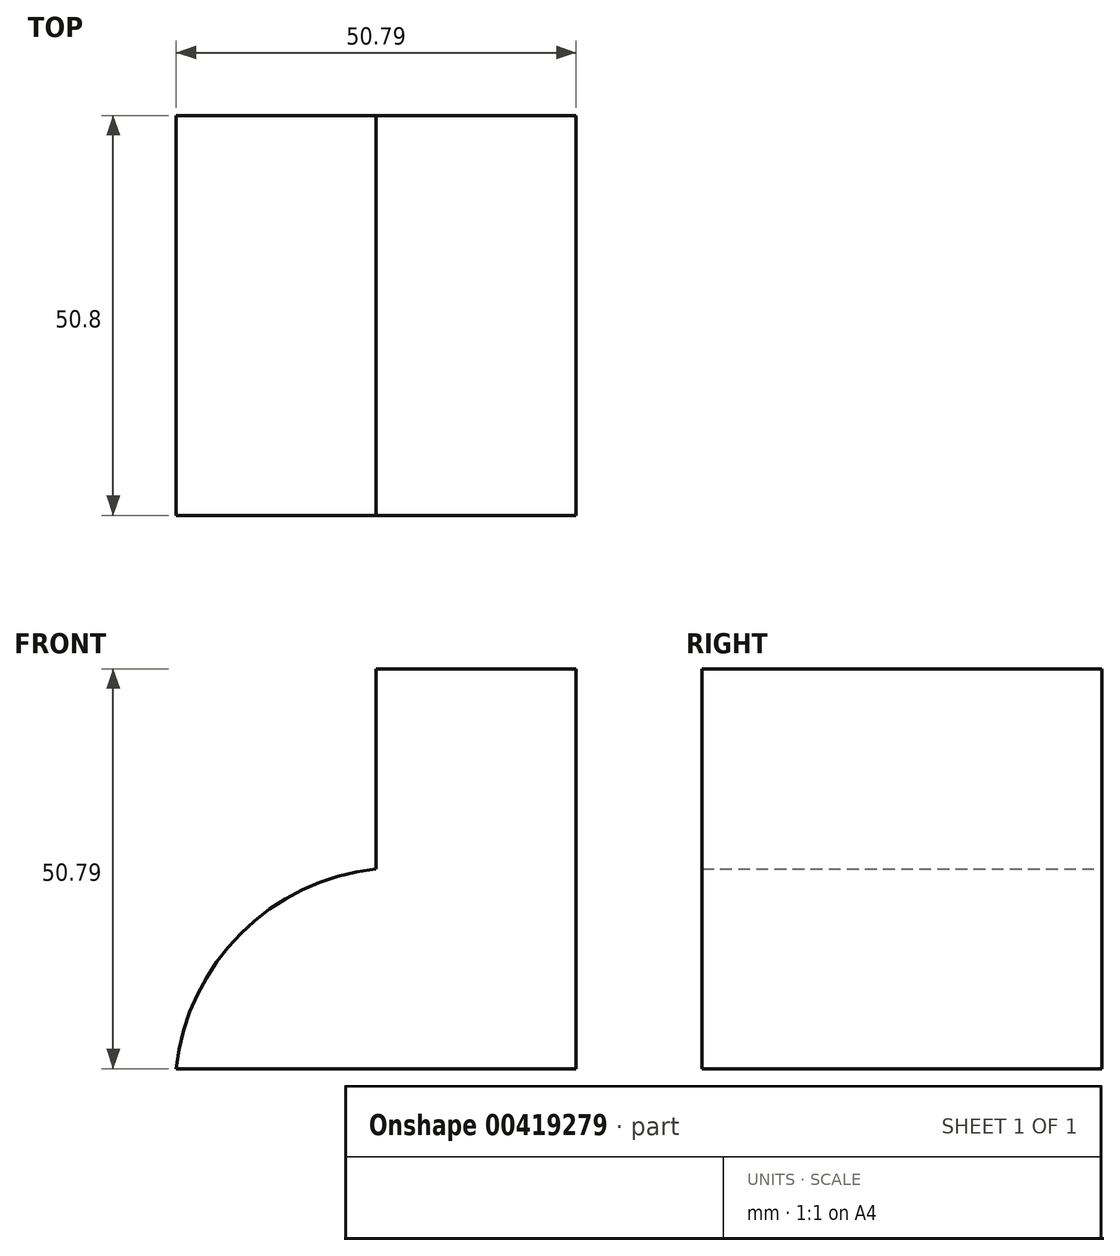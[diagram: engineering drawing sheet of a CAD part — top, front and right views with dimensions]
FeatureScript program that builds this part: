
annotation { "Feature Type Name" : "Feature", "Feature Type Description" : "" }
export const myFeature = defineFeature(function(context is Context, id is Id, definition is map)
    precondition{}
    {
        {
            var Q0;
            Q0=qCreatedBy(makeId("Front.planeOp"),FACE);
            var sketch = newSketch(context, id + "F0", { "sketchPlane" : qUnion([Q0])});
            skLineSegment(sketch, "E0", {"start": v(0, 0) * mm, "end": v(0, 50.8) * mm});
            skLineSegment(sketch, "E1", {"start": v(0, 0) * mm, "end": v(-50.8, 0) * mm});
            skLineSegment(sketch, "E2", {"start": v(0, 50.8) * mm, "end": v(-25.4, 50.8) * mm});
            skLineSegment(sketch, "E3", {"start": v(-25.4, 50.8) * mm, "end": v(-25.4, 25.4) * mm});
            skArc(sketch, "E4", {"start": v(-25.4, 25.4) * mm, "mid": v(-42.58, 17.18) * mm, "end": v(-50.8, 0) * mm});
            skSolve(sketch);
        }
        {
            var Q0;
            Q0=makeQuery(id+"F0.imprint","IMPRINT",FACE,{"disambiguationData":[TD([[makeQuery(id+"F0.imprint","IMPRINT",EDGE,{"derivedFrom":sQuery(id+"F0.wireOp",EDGE,"E0")}),1.0]])]});
            extrude(context, id + "F1", {"entities" : qUnion([Q0]), "depth" : 50.8 * mm});
        }
    });
